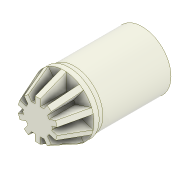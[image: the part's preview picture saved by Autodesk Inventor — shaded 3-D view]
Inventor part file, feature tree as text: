
AUTODESK INVENTOR PART (.ipt)
format: ipt  version: 2022 (Build 260153000, 153)  size: 250,368 bytes
history: native  units: mm
features: sketch x7, extrude x6, thicken_offset x2, chamfer x1, hole x1, pattern_circular x1, fillet x1
ambient origin geometry x8: Origin, YZ Plane, XZ Plane, XY Plane, X Axis, Y Axis, Z Axis, Center Point
bodies: Solid1 (feature_tree)
feature tree (19):
  extrude  "Adapter"  Depth=1.0mm TaperAngle=0.0deg
  extrude  "Motor Shaft Profile"  Depth=13.0mm
  chamfer  "Chamfer1"  Distance=12.0mm
  thicken_offset  "Thicken5"
  thicken_offset  "Thicken6"
  hole  "Hole6"  [1 undecoded]
  extrude  "Extrusion5"  Depth=0.2mm
  extrude  "Extrusion6"  Depth=2.0mm
  extrude  "Extrusion7"  Depth=7.5mm
  pattern_circular  "Circular Pattern1"  [2 undecoded]
  extrude  "Extrusion8"  Depth=1.0mm TaperAngle=0.0deg
  fillet  "Fillet1"  [1 undecoded]
  sketch  "Sketch1"  dims[d1=11.0mm d2=1.0mm d3=0.0mm]
  sketch  "Sketch6"  dims[d4=13.0mm d5=0.0mm d35=6.0mm]
  sketch  "Sketch9"  dims[d36=5.5mm d37=12.0mm d38=0.0mm]
  sketch  "Sketch10"  dims[d39=0.2mm d40=0.1mm d48=0.5mm d49=2.0mm d50=45.0deg]
  sketch  "Sketch11"  dims[d58=0.2mm d59=0.2mm]
  sketch  "Sketch12"  dims[d67=2.85mm d68=7.0mm d69=4.0mm d70=2.0mm d71=90.0deg d72=10.4mm d73=20.594885mm d74=11.5mm]
  sketch  "Sketch13"  dims[d75=1.0mm d76=0.0mm d77=7.5mm d78=6.0mm d79=1.0mm d80=0.0mm d81=0.0mm d82=0.0mm d83=100.0mm d84=360.0deg d86=5.0mm d87=10.0mm d88=0.0mm d89=2.0mm d41=1.0mm d42=1.0mm d43=1.0mm d44=0.15mm d45=0.25mm d46=0.375mm d47=14.3117mm d51=0.75mm d52=0.375mm d60=0.5mm d61=0.872665mm]
note: 4 required parameter values undecoded (feature->parameter linkage not recoverable at this tier; creation-order binding heuristic only, values carry confidence <= 0.55)
